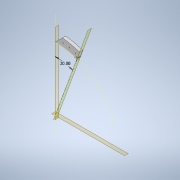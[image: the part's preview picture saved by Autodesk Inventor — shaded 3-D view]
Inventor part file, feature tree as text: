
AUTODESK INVENTOR PART (.ipt)
format: ipt  version: 2021.1 (Build 251245010, 245A)  size: 395,776 bytes
history: native  units: in
note: dims shown in document units (in); Inventor stores cm internally (conversion verified against a paired STEP export)
features: sketch x5, extrude x3, plane x2, emboss x1, split x1
ambient origin geometry x8: Origin, YZ Plane, XZ Plane, XY Plane, X Axis, Y Axis, Z Axis, Center Point
bodies: Solid1 (feature_tree)
feature tree (12):
  extrude  "Extrusion1"  Depth=0.35in
  extrude  "Extrusion2"  Depth=0.481in
  plane  "Work Plane1"
  emboss  "Emboss2"
  extrude  "Extrusion3"  Depth=1.0in
  sketch  "Sketch10"  dims[d8=0.75in d9=0.0in d11=45.0deg d12=0.201in d15=4.3307in d17=1.0in d18=0.3937in d20=1.0in d22=4.3307in d24=1.0in d25=0.3937in d27=1.0in d29=1.0in d30=0.0in d39=1.175in d40=0.201in d41=1.0in d42=4.7244in d44=60.0deg d46=0.0in d47=0.0in d48=0.1374in d49=90.0deg]
  plane  "Work Plane6"
  split  "Split2"
  sketch  "Sketch1"  dims[d0=40.0in d1=0.35in]
  sketch  "Sketch2"  dims[d2=2.0in d3=0.481in]
  sketch  "Sketch5"  dims[d4=1.0in d5=0.0in d6=0.125in]
  sketch  "Sketch8"  dims[d7=0.25in]
